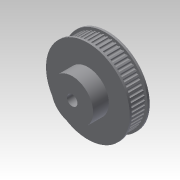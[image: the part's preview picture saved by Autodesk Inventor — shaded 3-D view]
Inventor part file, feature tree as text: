
AUTODESK INVENTOR PART (.ipt)
format: ipt  version: 2020 (Build 240168000, 168)  size: 244,224 bytes
history: native  units: mm
features: sketch x2, revolve x1, extrude x1, pattern_circular x1
ambient origin geometry x8: Origin, YZ Plane, XZ Plane, XY Plane, X Axis, Y Axis, Z Axis, Center Point
bodies: Solid1 (feature_tree)
feature tree (5):
  revolve  "Revolution1"  [1 undecoded]
  extrude  "Extrusion1"  Depth=18.85mm
  pattern_circular  "Circular Pattern1"  Angle=90.0deg  [1 undecoded]
  sketch  "Sketch1"  dims[d0=2.5mm d1=7.5mm]
  sketch  "Sketch2"  dims[d4=1.0mm d6=18.85mm d7=90.0deg d8=1.3mm d9=18.85mm d10=10.0mm d11=0.0mm d12=600.0mm d13=360.0deg d15=20.0mm d16=7.5mm d17=10.0mm]
note: 2 required parameter values undecoded (feature->parameter linkage not recoverable at this tier; creation-order binding heuristic only, values carry confidence <= 0.55)